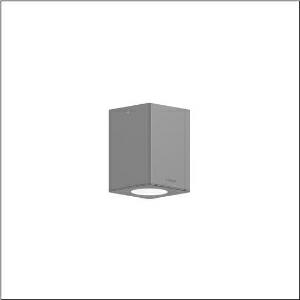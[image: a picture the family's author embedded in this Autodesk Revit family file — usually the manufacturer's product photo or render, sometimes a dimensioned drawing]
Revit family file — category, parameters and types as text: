
# Revit family: cl_31_decke_5cl613603
name_source: partatom
category: Lighting Fixtures
units: mm (PartAtom-declared; Revit-internal decimal feet)

## family parameters
Cut with Voids When Loaded = No
Host = Face
Light Source = No
Part Type = Normal
Room Calculation Point = No
Round Connector Dimension = Use Diameter
Shared = No

## types (1)
- --- (1 x LED, 1500 lm, 15 W, 3000K)
    Apparent Load = 15 VA
    CIE Flux Codes = 98 100 100 100 100
    Color Rendering = 80
    Color Temperature = 3000K
    Default Elevation = 1800 mm
    Description = CL 31 Ceiling, ceiling luminaire, primary light control with reflector, of aluminium, primary optical cover: cover panel, of glass, transparent, primary light characteristic: symmetric, installation type: surface-mounted, LED, rated luminous flux: 1.500lm, luminous efficacy: 100lm/W, light colour: 830, colour temperature: 3000K, control gear: DALI, with terminal, 5-pole, max. 2.5mm², mains connection: 220..240V, AC, 50/60Hz, rated input power: 15W, luminaire housing, of aluminium, powder-coated, SITECO metallic grey, length: 120mm, width: 120mm, height: 165mm, protection rating (complete): IP65, insulation class (complete): insulation class I (protective earthing), certification: CE, ENEC, impact resistance: IK09, permissible operating ambient temperature for outdoor applications: -20..+50°C, packaging unit: 1 piece
    Height = 166 mm
    Lamp = 1 x LED
    Lamp Light Flux = 1500 lm
    Lamp Power = 15 W
    Lamp count = 1
    Length = 120 mm
    Luminous efficacy = 100 lm/W
    Manufacturer = Siteco
    ModVariant = No
    Model = 5CL613603
    Mounting Place = Ceiling
    Mounting Type = Surface mounted
    Number of Poles = 1
    OnlyDefault = Yes
    Power Factor = 1
    Product Name = CL 31 Decke
    Product group = ceiling luminaire
    ProductGroupID = 308
    Protection Class = Protection class I
    Protection Degree = IP 65
    RLX_Detail_Level = 1
    RLX_Emergency_Light_Flux = 0 lm
    RLX_Emergency_Type = 0
    RLX_Emergency_Type_DB = No
    RlxData = <blob elided: 33165 chars, md5=779b9371>
    Socket = socket
    Standby Power = 0 W
    System Light Flux = 1500 lm
    System Power = 15 W
    Type Comments = factory setting: luminous flux: 100 % | dim-lin: 254 | 348 mA
    Type Image = l_1006909.jpg
    URL = http://relux.com
    VarID = @adj_192943
    Voltage = 0 V
    Weight = 0.00 kg
    Width = 120 mm

## geometry (parser evidence)
native form markers: Blend x4, Sweep x11
no freeform markers — native parametric forms only
